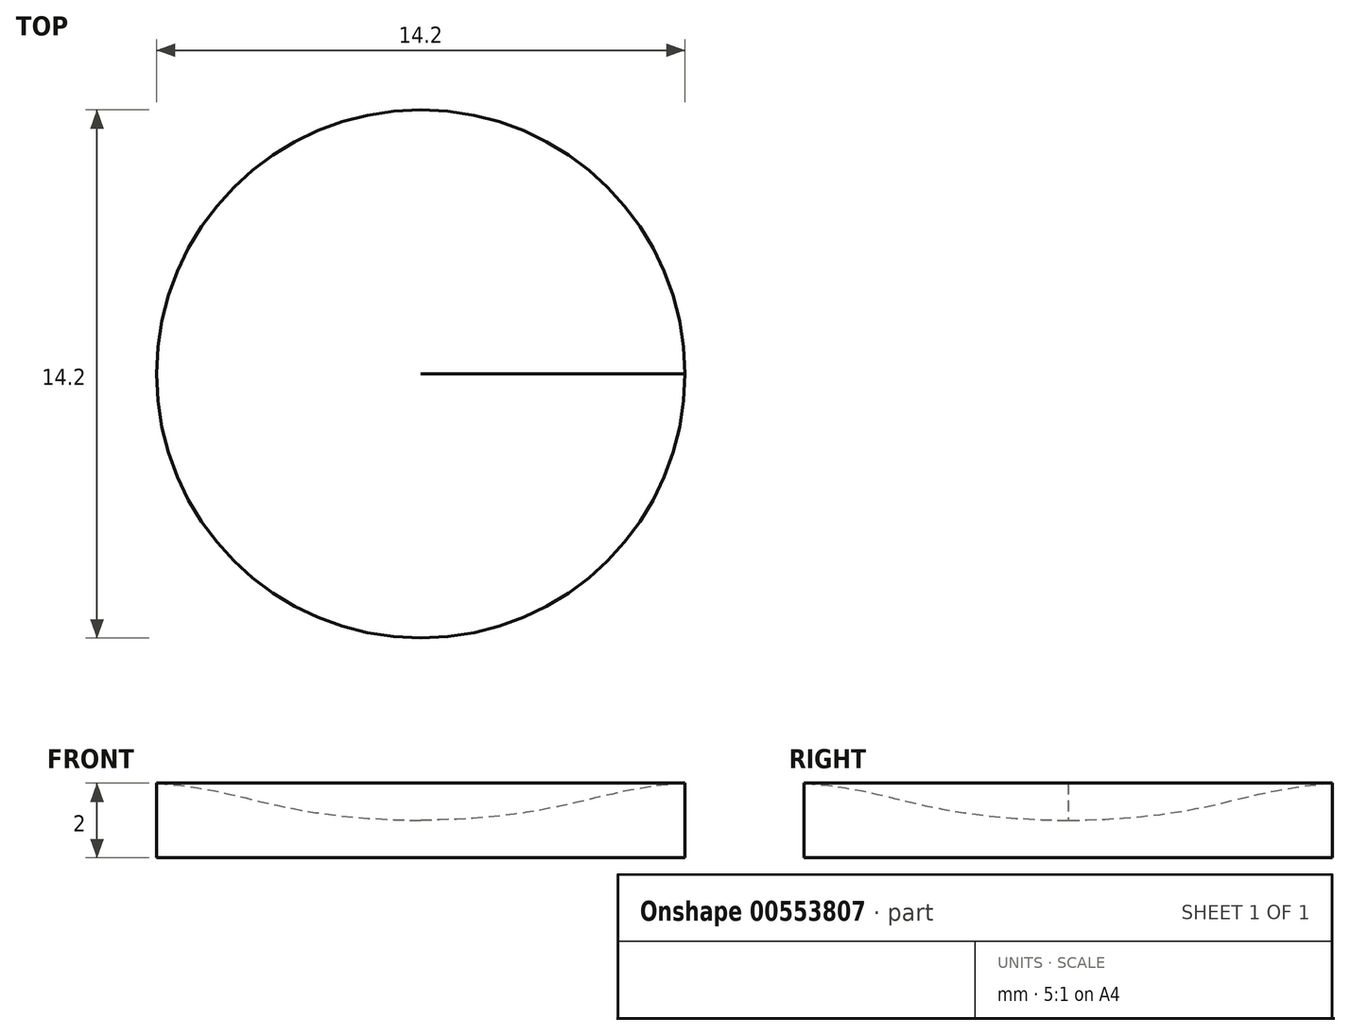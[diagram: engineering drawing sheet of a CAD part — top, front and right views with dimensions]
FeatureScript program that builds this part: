
annotation { "Feature Type Name" : "Feature", "Feature Type Description" : "" }
export const myFeature = defineFeature(function(context is Context, id is Id, definition is map)
    precondition{}
    {
        {
            var Q0;
            Q0=qCreatedBy(makeId("Front.planeOp"),FACE);
            var sketch = newSketch(context, id + "F0", { "sketchPlane" : qUnion([Q0])});
            skLineSegment(sketch, "E0", {"start": v(0, 0) * mm, "end": v(7.1, 0) * mm});
            skLineSegment(sketch, "E1", {"start": v(7.1, 0) * mm, "end": v(7.1, 2) * mm});
            skLineSegment(sketch, "E2", {"start": v(0, 1) * mm, "end": v(0, 0) * mm});
            skFitSpline(sketch, "E3", {"points": [v(7.1, 2) * mm, v(0, 1) * mm], "startDerivative": vector(-7.89, -0.57) * mm, "endDerivative": vector(-12, -0.18) * mm});
            skPoint(sketch, "E4.orphan", {"position": v(0, 2) * mm});
            skSolve(sketch);
        }
        {
            var Q0;
            Q0=makeQuery(id+"F0.imprint","IMPRINT",FACE,{"disambiguationData":[TD([[makeQuery(id+"F0.imprint","IMPRINT",EDGE,{"derivedFrom":sQuery(id+"F0.wireOp",EDGE,"E0")}),1.0]])]});
            var Q1;
            Q1=sQuery(id+"F0.wireOp",EDGE,"E2");
            revolve(context, id + "F1", {"entities" : qUnion([Q0]), "axis" : qUnion([Q1]), "revolveType" : RevolveType.FULL});
        }
    });
